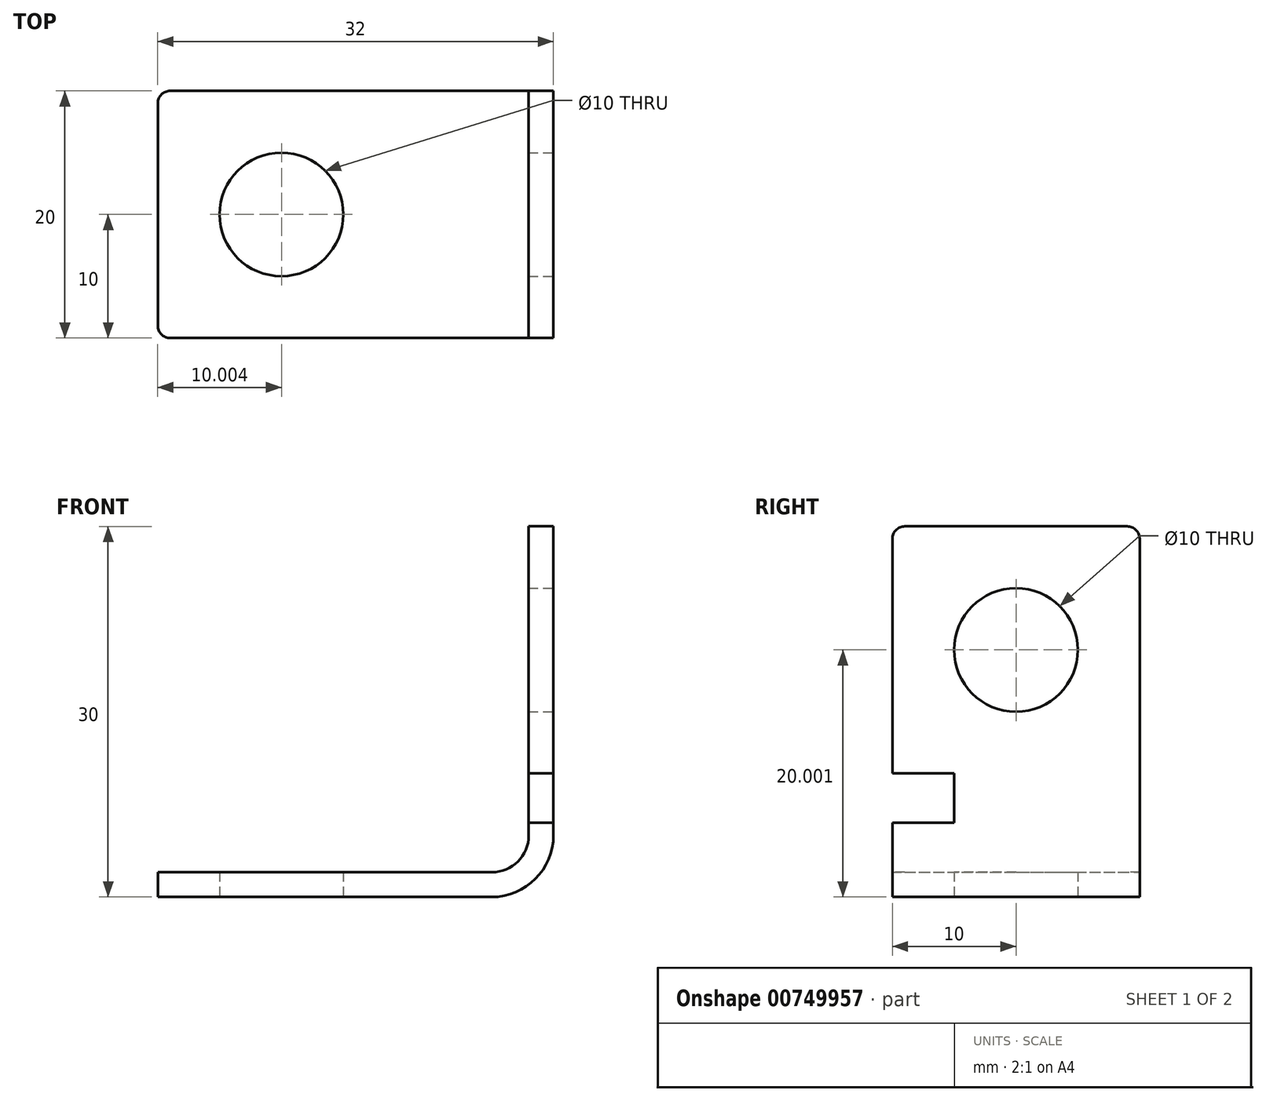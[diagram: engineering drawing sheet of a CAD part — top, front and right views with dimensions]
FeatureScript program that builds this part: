
annotation { "Feature Type Name" : "Feature", "Feature Type Description" : "" }
export const myFeature = defineFeature(function(context is Context, id is Id, definition is map)
    precondition{}
    {
        {
            var Q0;
            Q0=qCreatedBy(makeId("Front.planeOp"),FACE);
            var sketch = newSketch(context, id + "F0", { "sketchPlane" : qUnion([Q0])});
            skLineSegment(sketch, "E0", {"start": v(-56.36, -32.14) * mm, "end": v(-29.36, -32.14) * mm});
            skLineSegment(sketch, "E1", {"start": v(-26.36, -29.14) * mm, "end": v(-26.36, -4.14) * mm});
            skPoint(sketch, "E2.visualSharp", {"position": v(-26.36, -32.14) * mm});
            skArc(sketch, "E2.filletArc", {"start": v(-29.36, -32.14) * mm, "mid": v(-27.23, -31.26) * mm, "end": v(-26.36, -29.14) * mm});
            skLineSegment(sketch, "E3.0", {"start": v(-24.36, -29.14) * mm, "end": v(-24.36, -4.14) * mm});
            skArc(sketch, "E3.1", {"start": v(-29.36, -34.14) * mm, "mid": v(-25.82, -32.67) * mm, "end": v(-24.36, -29.14) * mm});
            skLineSegment(sketch, "E3.2", {"start": v(-56.36, -34.14) * mm, "end": v(-29.36, -34.14) * mm});
            skLineSegment(sketch, "E4", {"start": v(-56.36, -32.14) * mm, "end": v(-56.36, -34.14) * mm});
            skLineSegment(sketch, "E5", {"start": v(-26.36, -4.14) * mm, "end": v(-24.36, -4.14) * mm});
            skSolve(sketch);
        }
        {
            var Q0;
            Q0 = qSketchRegion(id + "F0", true);
            extrude(context, id + "F1", {"entities" : qUnion([Q0]), "depth" : 20 * mm, "offsetDistance" : 25 * mm});
        }
        {
            var Q0;
            Q0=makeQuery(id+"F1.opExtrude","SWEPT_FACE",FACE,{"disambiguationData":[OSD([sQuery(id+"F0.wireOp",EDGE,"E3.0")])]});
            var sketch = newSketch(context, id + "F2", { "sketchPlane" : qUnion([Q0])});
            skLineSegment(sketch, "E6", {"start": v(-17.19, -4.14) * mm, "end": v(-17.19, -24.14) * mm});
            skLineSegment(sketch, "E7", {"start": v(-20, -24.14) * mm, "end": v(-15, -24.14) * mm});
            skLineSegment(sketch, "E8", {"start": v(-15, -24.14) * mm, "end": v(-15, -28.14) * mm});
            skLineSegment(sketch, "E9", {"start": v(-15, -28.14) * mm, "end": v(-20, -28.14) * mm});
            skLineSegment(sketch, "E10", {"start": v(-20, -28.14) * mm, "end": v(-20, -24.14) * mm});
            skSolve(sketch);
        }
        {
            var Q0;
            Q0 = qSketchRegion(id + "F2", true);
            extrude(context, id + "F3", {"entities" : qUnion([Q0]), "operationType" : NewBodyOperationType.REMOVE, "oppositeDirection" : true, "depth" : 3 * mm, "offsetDistance" : 25 * mm});
        }
        {
            var Q0;
            Q0=makeQuery(id+"F1.opExtrude","SWEPT_FACE",FACE,{"disambiguationData":[OSD([sQuery(id+"F0.wireOp",EDGE,"E3.0")])]});
            var sketch = newSketch(context, id + "F4", { "sketchPlane" : qUnion([Q0])});
            skCircle(sketch, "E11", {"center": v(-10, -14.14) * mm, "radius": 5 * mm});
            skSolve(sketch);
        }
        {
            var Q0;
            Q0 = qSketchRegion(id + "F4", true);
            extrude(context, id + "F5", {"entities" : qUnion([Q0]), "operationType" : NewBodyOperationType.REMOVE, "oppositeDirection" : true, "depth" : 3 * mm, "offsetDistance" : 25 * mm});
        }
        {
            var Q0;
            Q0=makeQuery(id+"F1.opExtrude","SWEPT_FACE",FACE,{"disambiguationData":[OSD([sQuery(id+"F0.wireOp",EDGE,"E3.2")])]});
            var sketch = newSketch(context, id + "F6", { "sketchPlane" : qUnion([Q0])});
            skCircle(sketch, "E12", {"center": v(-46.36, 10) * mm, "radius": 5 * mm});
            skSolve(sketch);
        }
        {
            var Q0;
            Q0 = qSketchRegion(id + "F6", true);
            extrude(context, id + "F7", {"entities" : qUnion([Q0]), "operationType" : NewBodyOperationType.REMOVE, "oppositeDirection" : true, "depth" : 3 * mm, "offsetDistance" : 25 * mm});
        }
        {
            var Q0;
            Q0=makeQuery(id+"F1.opExtrude","CAP_EDGE",EDGE,{"disambiguationData":[OSD([sQuery(id+"F0.wireOp",EDGE,"E5")])],"isStart":false});
            var Q1;
            Q1=makeQuery(id+"F1.opExtrude","CAP_EDGE",EDGE,{"disambiguationData":[OSD([sQuery(id+"F0.wireOp",EDGE,"E5")])],"isStart":true});
            var Q2;
            Q2=makeQuery(id+"F1.opExtrude","CAP_EDGE",EDGE,{"disambiguationData":[OSD([sQuery(id+"F0.wireOp",EDGE,"E4")])],"isStart":false});
            var Q3;
            Q3=makeQuery(id+"F1.opExtrude","CAP_EDGE",EDGE,{"disambiguationData":[OSD([sQuery(id+"F0.wireOp",EDGE,"E4")])],"isStart":true});
            fillet(context, id + "F8", {"entities" : qUnion([Q0, Q1, Q2, Q3]), "radius" : 1 * mm, "tangentPropagation" : true, "allowEdgeOverflow" : false});
        }
    });
